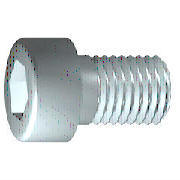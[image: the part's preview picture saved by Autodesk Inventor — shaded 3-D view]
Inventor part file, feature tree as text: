
AUTODESK INVENTOR PART (.ipt)
format: ipt  version: 2022 (Build 260153000, 153)  size: 198,656 bytes
history: native  units: mm (DEFAULTED — no unit token found)
features: sketch x2, extrude x1, plane x1, fillet x1
ambient origin geometry x7: Origin, YZ Plane, XY Plane, X Axis, Y Axis, Z Axis, Center Point
bodies: Solid1 (feature_tree), Body (feature_tree)
feature tree (5):
  extrude  "Slot"  Depth=6.0mm
  plane  "Work Plane1"
  fillet  "Fillet2"  Radius=6.0mm
  sketch  "Sketch1"  dims[d1=7.5mm d2=0.61355mm d3=6.0mm]
  sketch  "Sketch2"  dims[d4=3.0mm d5=60.0deg d6=6.0mm d7=6.0mm d8=5.773503mm d9=10.0mm d10=90.0deg d11=10.0mm d12=0.0mm d13=7.5mm d14=0.0mm d15=0.61345mm d16=0.61345mm d17=0.6mm d19=0.0mm d26=10.0mm d27=45.0deg d28=0.0mm d29=0.0mm d30=0.1mm]
